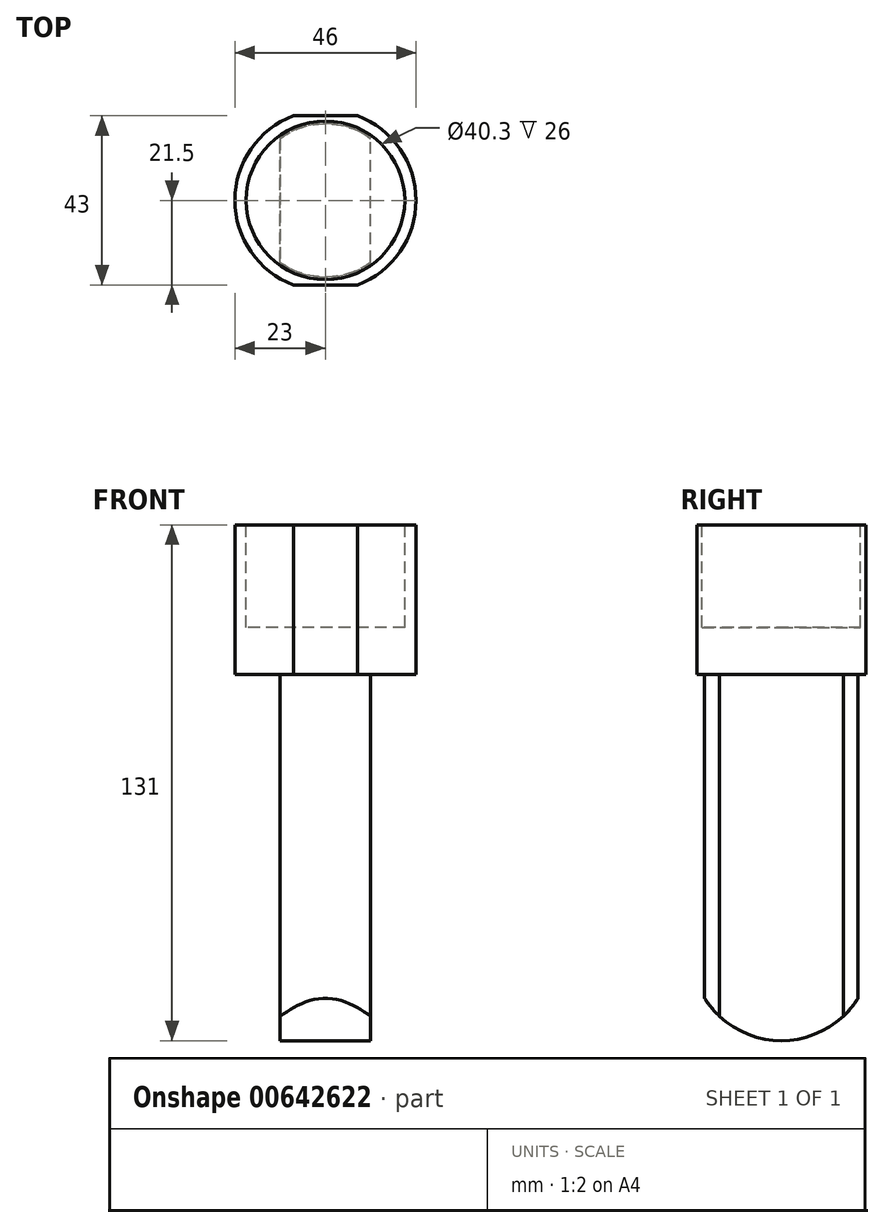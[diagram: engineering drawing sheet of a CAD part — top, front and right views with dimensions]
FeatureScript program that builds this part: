
annotation { "Feature Type Name" : "Feature", "Feature Type Description" : "" }
export const myFeature = defineFeature(function(context is Context, id is Id, definition is map)
    precondition{}
    {
        {
            var Q0;
            Q0=qCreatedBy(makeId("Top.planeOp"),FACE);
            var sketch = newSketch(context, id + "F0", { "sketchPlane" : qUnion([Q0])});
            skArc(sketch, "E0", {"start": v(8.17, -21.5) * mm, "mid": v(23, 0) * mm, "end": v(8.17, 21.5) * mm});
            skLineSegment(sketch, "E1", {"start": v(-8.17, -21.5) * mm, "end": v(8.17, -21.5) * mm});
            skLineSegment(sketch, "E2.MirrorCS", {"start": v(-8.17, 21.5) * mm, "end": v(8.17, 21.5) * mm});
            skArc(sketch, "E3.trimOffspring", {"start": v(-8.17, 21.5) * mm, "mid": v(-23, 0) * mm, "end": v(-8.17, -21.5) * mm});
            skSolve(sketch);
        }
        {
            var Q0;
            Q0 = qSketchRegion(id + "F0", true);
            extrude(context, id + "F1", {"entities" : qUnion([Q0]), "depth" : 38 * mm, "offsetDistance" : 25 * mm});
        }
        {
            var Q0;
            Q0=makeQuery(id+"F1.opExtrude","CAP_FACE",FACE,{"disambiguationData":[OSD([sQuery(id+"F0.wireOp",EDGE,"E0"),sQuery(id+"F0.wireOp",EDGE,"E1"),sQuery(id+"F0.wireOp",EDGE,"E2.MirrorCS"),sQuery(id+"F0.wireOp",EDGE,"E3.trimOffspring")])],"isStart":false});
            var sketch = newSketch(context, id + "F2", { "sketchPlane" : qUnion([Q0])});
            skCircle(sketch, "E4", {"center": v(0, 0) * mm, "radius": 20.15 * mm});
            skSolve(sketch);
        }
        {
            var Q0;
            Q0=makeQuery(id+"F2.imprint","IMPRINT",FACE,{"disambiguationData":[TD([[makeQuery(id+"F2.imprint","IMPRINT",EDGE,{"derivedFrom":sQuery(id+"F2.wireOp",EDGE,"E4")}),1.0]])]});
            var Q1;
            Q1=makeQuery(id+"F1.opExtrude","CAP_FACE",FACE,{"disambiguationData":[OSD([sQuery(id+"F0.wireOp",EDGE,"E0"),sQuery(id+"F0.wireOp",EDGE,"E1"),sQuery(id+"F0.wireOp",EDGE,"E2.MirrorCS"),sQuery(id+"F0.wireOp",EDGE,"E3.trimOffspring")])],"isStart":true});
            var Q2;
            Q2=sQuery(id+"F2.wireOp",EDGE,"E4");
            extrude(context, id + "F3", {"entities" : qUnion([Q0, Q1]), "operationType" : NewBodyOperationType.REMOVE, "surfaceEntities" : qUnion([Q2]), "oppositeDirection" : true, "depth" : 26 * mm, "offsetDistance" : 25 * mm});
        }
        {
            var Q0;
            Q0=makeQuery(id+"F1.opExtrude","CAP_FACE",FACE,{"disambiguationData":[OSD([sQuery(id+"F0.wireOp",EDGE,"E0"),sQuery(id+"F0.wireOp",EDGE,"E1"),sQuery(id+"F0.wireOp",EDGE,"E2.MirrorCS"),sQuery(id+"F0.wireOp",EDGE,"E3.trimOffspring")])],"isStart":true});
            var sketch = newSketch(context, id + "F4", { "sketchPlane" : qUnion([Q0])});
            skArc(sketch, "E5", {"start": v(-11.5, -15.75) * mm, "mid": v(0, -19.5) * mm, "end": v(11.5, -15.75) * mm});
            skLineSegment(sketch, "E6", {"start": v(-11.5, 15.75) * mm, "end": v(-11.5, -15.75) * mm});
            skLineSegment(sketch, "E7.MirrorCS", {"start": v(11.5, 15.75) * mm, "end": v(11.5, -15.75) * mm});
            skArc(sketch, "E8.trimOffspring", {"start": v(11.5, 15.75) * mm, "mid": v(0, 19.5) * mm, "end": v(-11.5, 15.75) * mm});
            skSolve(sketch);
        }
        {
            var Q0;
            Q0 = qSketchRegion(id + "F4", true);
            extrude(context, id + "F5", {"entities" : qUnion([Q0]), "operationType" : NewBodyOperationType.ADD, "depth" : 93 * mm, "offsetDistance" : 25 * mm});
        }
        {
            var Q0;
            Q0=makeQuery(id+"F5.opExtrude","SWEPT_FACE",FACE,{"disambiguationData":[OSD([sQuery(id+"F4.wireOp",EDGE,"E6")])]});
            var sketch = newSketch(context, id + "F6", { "sketchPlane" : qUnion([Q0])});
            skArc(sketch, "E9", {"start": v(-19.6, -82.03) * mm, "mid": v(-0.09, -93) * mm, "end": v(19.51, -82.18) * mm});
            skLineSegment(sketch, "E10", {"start": v(-19.6, -82.03) * mm, "end": v(-28.53, -100.05) * mm});
            skLineSegment(sketch, "E11", {"start": v(-28.53, -100.05) * mm, "end": v(50.8, -100.05) * mm});
            skLineSegment(sketch, "E12", {"start": v(50.8, -100.05) * mm, "end": v(19.51, -82.18) * mm});
            skSolve(sketch);
        }
        {
            var Q0;
            Q0 = qSketchRegion(id + "F6", true);
            extrude(context, id + "F7", {"entities" : qUnion([Q0]), "operationType" : NewBodyOperationType.REMOVE, "endBound" : BoundingType.THROUGH_ALL, "oppositeDirection" : true, "depth" : 25 * mm, "offsetDistance" : 25 * mm});
        }
    });
